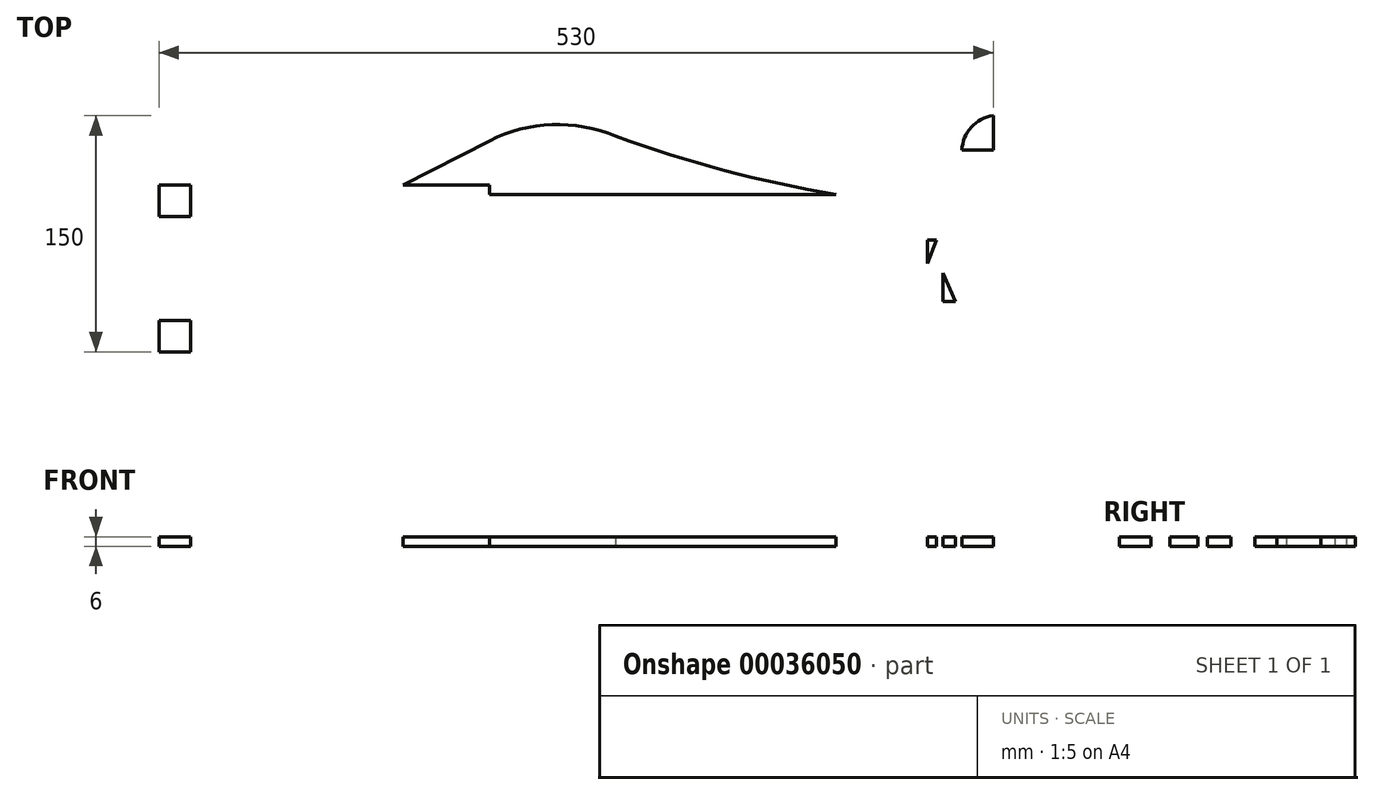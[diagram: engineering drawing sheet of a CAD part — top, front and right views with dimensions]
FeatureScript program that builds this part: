
annotation { "Feature Type Name" : "Feature", "Feature Type Description" : "" }
export const myFeature = defineFeature(function(context is Context, id is Id, definition is map)
    precondition{}
    {
        {
            var Q0;
            Q0=qCreatedBy(makeId("Top.planeOp"),FACE);
            var sketch = newSketch(context, id + "F0", { "sketchPlane" : qUnion([Q0])});
            skLineSegment(sketch, "E0.rect.bottom", {"start": v(-317.5, -75) * mm, "end": v(317.5, -75) * mm});
            skLineSegment(sketch, "E0.rect.top", {"start": v(-317.5, 75) * mm, "end": v(317.5, 75) * mm});
            skLineSegment(sketch, "E0.rect.left", {"start": v(-317.5, -75) * mm, "end": v(-317.5, 75) * mm});
            skLineSegment(sketch, "E0.rect.right", {"start": v(317.5, -75) * mm, "end": v(317.5, 75) * mm});
            skPoint(sketch, "E0.rect.middle", {"position": v(0, 0) * mm});
            skLineSegment(sketch, "E1", {"start": v(317.5, -75) * mm, "end": v(212.5, -75) * mm});
            skLineSegment(sketch, "E2", {"start": v(212.5, -75) * mm, "end": v(212.5, 53) * mm});
            skLineSegment(sketch, "E3.bottom", {"start": v(-317.5, -75) * mm, "end": v(-162.5, -75) * mm});
            skLineSegment(sketch, "E3.top", {"start": v(-317.5, 31) * mm, "end": v(-162.5, 31) * mm});
            skLineSegment(sketch, "E3.left", {"start": v(-317.5, -75) * mm, "end": v(-317.5, 31) * mm});
            skLineSegment(sketch, "E3.right", {"start": v(-162.5, -75) * mm, "end": v(-162.5, 31) * mm});
            skLineSegment(sketch, "E4", {"start": v(-317.5, -22) * mm, "end": v(148.5, -22) * mm});
            skPoint(sketch, "E4.endSnap0", {"position": v(-317.5, -22) * mm});
            skLineSegment(sketch, "E5", {"start": v(148.5, -22) * mm, "end": v(-31.5, -22) * mm});
            skLineSegment(sketch, "E6", {"start": v(-31.5, -22) * mm, "end": v(-251.5, -22) * mm});
            skLineSegment(sketch, "E7", {"start": v(-251.5, -22) * mm, "end": v(-317.5, -22) * mm});
            skLineSegment(sketch, "E8.bottom", {"start": v(-317.5, -22) * mm, "end": v(-309.5, -22) * mm});
            skLineSegment(sketch, "E8.top", {"start": v(-317.5, -5) * mm, "end": v(-309.5, -5) * mm});
            skLineSegment(sketch, "E8.left", {"start": v(-317.5, -22) * mm, "end": v(-317.5, -5) * mm});
            skLineSegment(sketch, "E8.right", {"start": v(-309.5, -22) * mm, "end": v(-309.5, -5) * mm});
            skLineSegment(sketch, "E9.top", {"start": v(-317.5, -39) * mm, "end": v(-309.5, -39) * mm});
            skLineSegment(sketch, "E9.left", {"start": v(-317.5, -22) * mm, "end": v(-317.5, -39) * mm});
            skLineSegment(sketch, "E9.right", {"start": v(-309.5, -22) * mm, "end": v(-309.5, -39) * mm});
            skLineSegment(sketch, "E10.rect.bottom", {"start": v(-31.5, -25) * mm, "end": v(-251.5, -25) * mm});
            skLineSegment(sketch, "E10.rect.top", {"start": v(-31.5, -19) * mm, "end": v(-251.5, -19) * mm});
            skLineSegment(sketch, "E10.rect.left", {"start": v(-31.5, -25) * mm, "end": v(-31.5, -19) * mm});
            skLineSegment(sketch, "E10.rect.right", {"start": v(-251.5, -25) * mm, "end": v(-251.5, -19) * mm});
            skPoint(sketch, "E10.rect.middle", {"position": v(-141.5, -22) * mm});
            skLineSegment(sketch, "E11.bottom", {"start": v(-162.5, 31) * mm, "end": v(-107.5, 31) * mm});
            skLineSegment(sketch, "E11.top", {"start": v(-162.5, 59) * mm, "end": v(-107.5, 59) * mm});
            skLineSegment(sketch, "E11.left", {"start": v(-162.5, 31) * mm, "end": v(-162.5, 59) * mm});
            skLineSegment(sketch, "E11.right", {"start": v(-107.5, 31) * mm, "end": v(-107.5, 59) * mm});
            skLineSegment(sketch, "E12", {"start": v(-162.5, 31) * mm, "end": v(-107.5, 59) * mm});
            skLineSegment(sketch, "E13.bottom", {"start": v(-107.5, 31) * mm, "end": v(112.5, 31) * mm});
            skLineSegment(sketch, "E13.top", {"start": v(-107.5, 25) * mm, "end": v(112.5, 25) * mm});
            skLineSegment(sketch, "E13.left", {"start": v(-107.5, 31) * mm, "end": v(-107.5, 25) * mm});
            skLineSegment(sketch, "E13.right", {"start": v(112.5, 31) * mm, "end": v(112.5, 25) * mm});
            skLineSegment(sketch, "E14", {"start": v(112.5, 25) * mm, "end": v(150.5, 25) * mm});
            skLineSegment(sketch, "E15.bottom", {"start": v(-107.5, 59) * mm, "end": v(-27.5, 59) * mm});
            skLineSegment(sketch, "E15.top", {"start": v(-107.5, 62) * mm, "end": v(-27.5, 62) * mm});
            skLineSegment(sketch, "E15.left", {"start": v(-107.5, 59) * mm, "end": v(-107.5, 62) * mm});
            skLineSegment(sketch, "E15.right", {"start": v(-27.5, 59) * mm, "end": v(-27.5, 62) * mm});
            skArc(sketch, "E16", {"start": v(-27.5, 62) * mm, "mid": v(-67.83, 69.3) * mm, "end": v(-107.5, 59) * mm});
            skLineSegment(sketch, "E17", {"start": v(212.5, 53) * mm, "end": v(192.5, 53) * mm});
            skLineSegment(sketch, "E18", {"start": v(212.5, 53) * mm, "end": v(212.5, 75) * mm});
            skArc(sketch, "E19", {"start": v(212.5, 75) * mm, "mid": v(198.5, 67.64) * mm, "end": v(192.5, 53) * mm});
            skArc(sketch, "E20", {"start": v(150.5, 25) * mm, "mid": v(175.74, 32.64) * mm, "end": v(192.5, 53) * mm});
            skLineSegment(sketch, "E21", {"start": v(317.5, 75) * mm, "end": v(282.5, 75) * mm});
            skLineSegment(sketch, "E22.left", {"start": v(317.5, 75) * mm, "end": v(317.5, 50) * mm});
            skLineSegment(sketch, "E23", {"start": v(282.5, 75) * mm, "end": v(257.5, 75) * mm});
            skLineSegment(sketch, "E24", {"start": v(282.5, 75) * mm, "end": v(288.18, 50.65) * mm});
            skLineSegment(sketch, "E25", {"start": v(288.18, 50.65) * mm, "end": v(317.5, -75) * mm});
            skArc(sketch, "E26", {"start": v(288.18, 50.65) * mm, "mid": v(277.08, 68.17) * mm, "end": v(257.5, 75) * mm});
            skLineSegment(sketch, "E27.bottom", {"start": v(212.5, 53) * mm, "end": v(191.84, 53) * mm});
            skLineSegment(sketch, "E27.top", {"start": v(212.5, 51.5) * mm, "end": v(191.84, 51.5) * mm});
            skLineSegment(sketch, "E27.left", {"start": v(212.5, 53) * mm, "end": v(212.5, 51.5) * mm});
            skLineSegment(sketch, "E27.right", {"start": v(191.84, 53) * mm, "end": v(191.84, 51.5) * mm});
            skLineSegment(sketch, "E28.bottom", {"start": v(212.5, -75) * mm, "end": v(213.5, -75) * mm});
            skLineSegment(sketch, "E28.top", {"start": v(212.5, -70) * mm, "end": v(213.5, -70) * mm});
            skLineSegment(sketch, "E28.left", {"start": v(212.5, -75) * mm, "end": v(212.5, -70) * mm});
            skLineSegment(sketch, "E28.right", {"start": v(213.5, -75) * mm, "end": v(213.5, -70) * mm});
            skLineSegment(sketch, "E29.bottom", {"start": v(-317.5, 31) * mm, "end": v(-297.5, 31) * mm});
            skLineSegment(sketch, "E29.top", {"start": v(-317.5, 11) * mm, "end": v(-297.5, 11) * mm});
            skLineSegment(sketch, "E29.left", {"start": v(-317.5, 31) * mm, "end": v(-317.5, 11) * mm});
            skLineSegment(sketch, "E29.right", {"start": v(-297.5, 31) * mm, "end": v(-297.5, 11) * mm});
            skLineSegment(sketch, "E30.bottom", {"start": v(-317.5, -75) * mm, "end": v(-297.5, -75) * mm});
            skLineSegment(sketch, "E30.top", {"start": v(-317.5, -55) * mm, "end": v(-297.5, -55) * mm});
            skLineSegment(sketch, "E30.left", {"start": v(-317.5, -75) * mm, "end": v(-317.5, -55) * mm});
            skLineSegment(sketch, "E30.right", {"start": v(-297.5, -75) * mm, "end": v(-297.5, -55) * mm});
            skArc(sketch, "E31", {"start": v(-297.5, 31) * mm, "mid": v(-311.64, 25.14) * mm, "end": v(-317.5, 11) * mm});
            skArc(sketch, "E32", {"start": v(-317.5, -55) * mm, "mid": v(-311.64, -69.14) * mm, "end": v(-297.5, -75) * mm});
            skLineSegment(sketch, "E33", {"start": v(148.5, -22) * mm, "end": v(148.5, -19) * mm});
            skLineSegment(sketch, "E34", {"start": v(148.5, -22) * mm, "end": v(148.5, -25) * mm});
            skLineSegment(sketch, "E35", {"start": v(148.5, -19) * mm, "end": v(170.5, -19) * mm});
            skLineSegment(sketch, "E36", {"start": v(148.5, -25) * mm, "end": v(180.5, -25) * mm});
            skLineSegment(sketch, "E37.bottom", {"start": v(170.5, -19) * mm, "end": v(176.5, -19) * mm});
            skLineSegment(sketch, "E37.top", {"start": v(170.5, -4) * mm, "end": v(176.5, -4) * mm});
            skLineSegment(sketch, "E37.left", {"start": v(170.5, -19) * mm, "end": v(170.5, -4) * mm});
            skLineSegment(sketch, "E37.right", {"start": v(176.5, -19) * mm, "end": v(176.5, -4) * mm});
            skLineSegment(sketch, "E38.bottom", {"start": v(180.5, -25) * mm, "end": v(188.5, -25) * mm});
            skLineSegment(sketch, "E38.top", {"start": v(180.5, -43) * mm, "end": v(188.5, -43) * mm});
            skLineSegment(sketch, "E38.left", {"start": v(180.5, -25) * mm, "end": v(180.5, -43) * mm});
            skLineSegment(sketch, "E38.right", {"start": v(188.5, -25) * mm, "end": v(188.5, -43) * mm});
            skLineSegment(sketch, "E39", {"start": v(180.5, -25) * mm, "end": v(188.5, -43) * mm});
            skLineSegment(sketch, "E40", {"start": v(176.5, -4) * mm, "end": v(170.5, -19) * mm});
            skLineSegment(sketch, "E41", {"start": v(148.5, -22) * mm, "end": v(212.5, -22) * mm});
            skLineSegment(sketch, "E42", {"start": v(212.5, -22) * mm, "end": v(202.5, -22) * mm});
            skArc(sketch, "E43", {"start": v(188.5, -43) * mm, "mid": v(201.72, -17.59) * mm, "end": v(176.5, -4) * mm});
            skArc(sketch, "E44", {"start": v(-27.5, 62) * mm, "mid": v(41.63, 40.22) * mm, "end": v(112.5, 25) * mm});
            skSolve(sketch);
        }
        {
            var Q0;
            {var subQ8=sQuery(id+"F0.wireOp",EDGE,"E3.top");Q0=makeQuery(id+"F0.imprint","IMPRINT",FACE,{"disambiguationData":[TD([[makeQuery(id+"F0.imprint","IMPRINT",EDGE,{"derivedFrom":subQ8}),-1.0]])]});}
            var Q1;
            Q1=makeQuery(id+"F0.imprint","IMPRINT",FACE,{"disambiguationData":[TD([[makeQuery(id+"F0.imprint","IMPRINT",EDGE,{"derivedFrom":sQuery(id+"F0.wireOp",EDGE,"E29.top")}),1.0]])]});
            var Q2;
            {var subQ8=sQuery(id+"F0.wireOp",EDGE,"E3.bottom");Q2=makeQuery(id+"F0.imprint","IMPRINT",FACE,{"disambiguationData":[TD([[makeQuery(id+"F0.imprint","IMPRINT",EDGE,{"derivedFrom":subQ8}),1.0]])]});}
            var Q3;
            Q3=makeQuery(id+"F0.imprint","IMPRINT",FACE,{"disambiguationData":[TD([[makeQuery(id+"F0.imprint","IMPRINT",EDGE,{"derivedFrom":sQuery(id+"F0.wireOp",EDGE,"E30.top")}),-1.0]])]});
            var Q4;
            {var subQ13=sQuery(id+"F0.wireOp",EDGE,"E0.rect.bottom");Q4=makeQuery(id+"F0.imprint","IMPRINT",FACE,{"disambiguationData":[TD([[makeQuery(id+"F0.imprint","IMPRINT",EDGE,{"derivedFrom":subQ13}),1.0]])]});}
            var Q5;
            Q5=makeQuery(id+"F0.imprint","IMPRINT",FACE,{"disambiguationData":[TD([[makeQuery(id+"F0.imprint","IMPRINT",EDGE,{"derivedFrom":sQuery(id+"F0.wireOp",EDGE,"E11.bottom")}),1.0]])]});
            var Q6;
            {var subQ4=sQuery(id+"F0.wireOp",EDGE,"E11.right");Q6=makeQuery(id+"F0.imprint","IMPRINT",FACE,{"disambiguationData":[TD([[makeQuery(id+"F0.imprint","IMPRINT",EDGE,{"derivedFrom":subQ4}),-1.0]])]});}
            var Q7;
            {var subQ3=sQuery(id+"F0.wireOp",EDGE,"E13.top");Q7=makeQuery(id+"F0.imprint","IMPRINT",FACE,{"disambiguationData":[TD([[makeQuery(id+"F0.imprint","IMPRINT",EDGE,{"derivedFrom":subQ3}),1.0]])]});}
            var Q8;
            {var subQ0=sQuery(id+"F0.wireOp",EDGE,"E16");var subQ1=sQuery(id+"F0.wireOp",EDGE,"E15.top");var subQ2=makeQuery(id+"F0.imprint","INTERSECT",VERTEX,{"derivedFrom":[subQ1,subQ0]});Q8=makeQuery(id+"F0.imprint","IMPRINT",FACE,{"disambiguationData":[TD([[makeQuery(id+"F0.imprint","IMPRINT",EDGE,{"disambiguationData":[TD([[subQ2,-1.0]])],"derivedFrom":subQ1}),1.0]])]});}
            var Q9;
            {var subQ3=sQuery(id+"F0.wireOp",EDGE,"E15.bottom");Q9=makeQuery(id+"F0.imprint","IMPRINT",FACE,{"disambiguationData":[TD([[makeQuery(id+"F0.imprint","IMPRINT",EDGE,{"derivedFrom":subQ3}),1.0]])]});}
            var Q10;
            Q10=makeQuery(id+"F0.imprint","IMPRINT",FACE,{"disambiguationData":[TD([[makeQuery(id+"F0.imprint","IMPRINT",EDGE,{"derivedFrom":sQuery(id+"F0.wireOp",EDGE,"E1")}),-1.0]])]});
            var Q11;
            {var subQ2=sQuery(id+"F0.wireOp",EDGE,"E18");Q11=makeQuery(id+"F0.imprint","IMPRINT",FACE,{"disambiguationData":[TD([[makeQuery(id+"F0.imprint","IMPRINT",EDGE,{"derivedFrom":subQ2}),1.0]])]});}
            var Q12;
            {var subQ13=sQuery(id+"F0.wireOp",EDGE,"E5");Q12=makeQuery(id+"F0.imprint","IMPRINT",FACE,{"disambiguationData":[TD([[makeQuery(id+"F0.imprint","IMPRINT",EDGE,{"derivedFrom":subQ13}),-1.0]])]});}
            var Q13;
            Q13=makeQuery(id+"F0.imprint","IMPRINT",FACE,{"disambiguationData":[TD([[makeQuery(id+"F0.imprint","IMPRINT",EDGE,{"derivedFrom":sQuery(id+"F0.wireOp",EDGE,"E37.top")}),-1.0]])]});
            var Q14;
            Q14=makeQuery(id+"F0.imprint","IMPRINT",FACE,{"disambiguationData":[TD([[makeQuery(id+"F0.imprint","IMPRINT",EDGE,{"derivedFrom":sQuery(id+"F0.wireOp",EDGE,"E38.top")}),1.0]])]});
            extrude(context, id + "F1", {"entities" : qUnion([Q0, Q1, Q2, Q3, Q4, Q5, Q6, Q7, Q8, Q9, Q10, Q11, Q12, Q13, Q14]), "depth" : 6 * mm});
        }
    });
